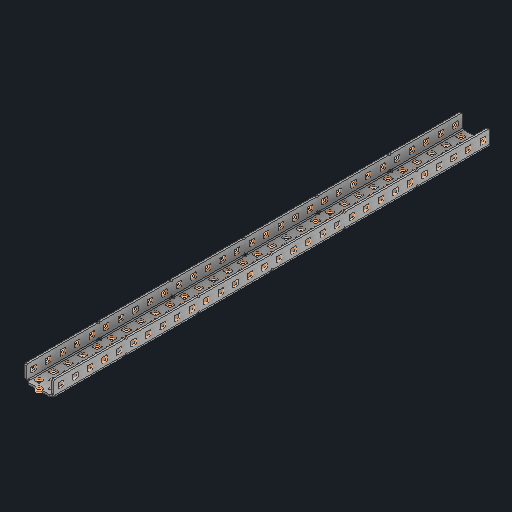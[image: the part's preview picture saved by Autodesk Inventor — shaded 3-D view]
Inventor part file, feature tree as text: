
AUTODESK INVENTOR PART (.ipt)
format: ipt  version: 2025 (Build 290162000, 162)  size: 2,433,536 bytes
history: native  units: in
note: dims shown in document units (in); Inventor stores cm internally (conversion verified against a paired STEP export)
features: other x306, sketch x5, sheet_metal_op x1
ambient origin geometry x8: Origin, YZ Plane, XZ Plane, XY Plane, X Axis, Y Axis, Z Axis, Center Point
bodies: Solid1 (feature_tree)
feature tree (312):
  other  "Alu C 1x2x1x30.ipt"
  other  "Solid1::Alu C 1x2x1x30.ipt"
  other  "TaggingFeature1"
  sketch  "Sketch1"  dims[d0=0.3937in]
  sketch  "Sketch2"  dims[d1=0.0625in]
  sketch  "Sketch3"
  other  "Flange Pattern Sketch"
  sketch  "Sketch9"
  sheet_metal_op  "Body Pattern Sketch"
  other  "Arc Length"
  sketch  "Sketch14"
  other  "Flange Pattern Plane"
  other  "Srf1"
  other  "Srf2"
  other  "Srf3"
  other  "Srf4"
  other  "Srf5"
  other  "Srf6"
  other  "Srf7"
  other  "Srf8"
  other  "Srf9"
  other  "Srf10"
  other  "Srf11"
  other  "Srf12"
  other  "Srf13"
  other  "Srf14"
  other  "Srf15"
  other  "Srf16"
  other  "Srf17"
  other  "Srf18"
  other  "Srf19"
  other  "Srf20"
  other  "Srf21"
  other  "Srf22"
  other  "Srf23"
  other  "Srf24"
  other  "Srf25"
  other  "Srf26"
  other  "Srf27"
  other  "Srf28"
  other  "Srf29"
  other  "Srf30"
  other  "Srf31"
  other  "Srf32"
  other  "Srf33"
  other  "Srf34"
  other  "Srf35"
  other  "Srf36"
  other  "Srf37"
  other  "Srf38"
  other  "Srf39"
  other  "Srf40"
  other  "Srf41"
  other  "Srf42"
  other  "Srf43"
  other  "Srf44"
  other  "Srf45"
  other  "Srf46"
  other  "Srf47"
  other  "Srf48"
  other  "Srf49"
  other  "Srf50"
  other  "Srf51"
  other  "Srf52"
  other  "Srf53"
  other  "Srf54"
  other  "Srf55"
  other  "Srf56"
  other  "Srf57"
  other  "Srf58"
  other  "Srf59"
  other  "Srf60"
  other  "Srf61"
  other  "Srf62"
  other  "Srf63"
  other  "Srf64"
  other  "Srf65"
  other  "Srf66"
  other  "Srf67"
  other  "Srf68"
  other  "Srf69"
  other  "Srf70"
  other  "Srf71"
  other  "Srf72"
  other  "Srf73"
  other  "Srf74"
  other  "Srf75"
  other  "Srf76"
  other  "Srf77"
  other  "Srf78"
  other  "Srf79"
  other  "Srf80"
  other  "Srf81"
  other  "Srf82"
  other  "Srf83"
  other  "Srf84"
  other  "Srf85"
  other  "Srf86"
  other  "Srf87"
  other  "Srf88"
  other  "Srf89"
  other  "Srf90"
  other  "Srf91"
  other  "Srf92"
  other  "Srf93"
  other  "Srf94"
  other  "Srf95"
  other  "Srf96"
  other  "Srf97"
  other  "Srf98"
  other  "Srf99"
  other  "Srf100"
  other  "Srf101"
  other  "Srf102"
  other  "Srf103"
  other  "Srf104"
  other  "Srf105"
  other  "Srf106"
  other  "Srf107"
  other  "Srf108"
  other  "Srf109"
  other  "Srf110"
  other  "Srf111"
  other  "Srf112"
  other  "Srf113"
  other  "Srf114"
  other  "Srf115"
  other  "Srf116"
  other  "Srf117"
  other  "Srf118"
  other  "Srf119"
  other  "Srf120"
  other  "Srf121"
  other  "Srf122"
  other  "Srf123"
  other  "Srf124"
  other  "Srf125"
  other  "Srf126"
  other  "Srf127"
  other  "Srf128"
  other  "Srf129"
  other  "Srf130"
  other  "Srf131"
  other  "Srf132"
  other  "Srf133"
  other  "Srf134"
  other  "Srf135"
  other  "Srf136"
  other  "Srf137"
  other  "Srf138"
  other  "Srf139"
  other  "Srf140"
  other  "Srf141"
  other  "Srf142"
  other  "Srf143"
  other  "Srf144"
  other  "Srf145"
  other  "Srf146"
  other  "Srf147"
  other  "Srf148"
  other  "Srf149"
  other  "Srf150"
  other  "Srf1::Derived"
  other  "Srf2::Derived"
  other  "Srf823::Derived"
  other  "Srf824::Derived"
  other  "Srf825::Derived"
  other  "Srf826::Derived"
  other  "Srf827::Derived"
  other  "Srf828::Derived"
  other  "Srf829::Derived"
  other  "Srf922::Derived"
  other  "Srf923::Derived"
  other  "Srf924::Derived"
  other  "Srf925::Derived"
  other  "Srf926::Derived"
  other  "Srf1143::Derived"
  other  "Srf1144::Derived"
  other  "Srf1145::Derived"
  other  "Srf1146::Derived"
  other  "Srf1147::Derived"
  other  "Srf1148::Derived"
  other  "Srf1149::Derived"
  other  "Srf1150::Derived"
  other  "Srf1151::Derived"
  other  "Srf1152::Derived"
  other  "Srf1153::Derived"
  other  "Srf1154::Derived"
  other  "Srf1155::Derived"
  other  "Srf1156::Derived"
  other  "Srf1157::Derived"
  other  "Srf1158::Derived"
  other  "Srf1159::Derived"
  other  "Srf1160::Derived"
  other  "Srf1161::Derived"
  other  "Srf1162::Derived"
  other  "Srf1163::Derived"
  other  "Srf1164::Derived"
  other  "Srf1165::Derived"
  other  "Srf1166::Derived"
  other  "Srf1167::Derived"
  other  "Srf1168::Derived"
  other  "Srf1169::Derived"
  other  "Srf1170::Derived"
  other  "Srf1171::Derived"
  other  "Srf1172::Derived"
  other  "Srf1173::Derived"
  other  "Srf1174::Derived"
  other  "Srf1175::Derived"
  other  "Srf1176::Derived"
  other  "Srf1177::Derived"
  other  "Srf1178::Derived"
  other  "Srf1179::Derived"
  other  "Srf1180::Derived"
  other  "Srf1181::Derived"
  other  "Srf1182::Derived"
  other  "Srf1183::Derived"
  other  "Srf1184::Derived"
  other  "Srf1185::Derived"
  other  "Srf1186::Derived"
  other  "Srf1187::Derived"
  other  "Srf1188::Derived"
  other  "Srf91::Derived"
  other  "Srf92::Derived"
  other  "Srf856::Derived"
  other  "Srf857::Derived"
  other  "Srf858::Derived"
  other  "Srf859::Derived"
  other  "Srf860::Derived"
  other  "Srf861::Derived"
  other  "Srf862::Derived"
  other  "Srf959::Derived"
  other  "Srf960::Derived"
  other  "Srf961::Derived"
  other  "Srf962::Derived"
  other  "Srf963::Derived"
  other  "Srf1199::Derived"
  other  "Srf1200::Derived"
  other  "Srf1201::Derived"
  other  "Srf1202::Derived"
  other  "Srf1203::Derived"
  other  "Srf1204::Derived"
  other  "Srf1205::Derived"
  other  "Srf1206::Derived"
  other  "Srf1207::Derived"
  other  "Srf1208::Derived"
  other  "Srf1209::Derived"
  other  "Srf1210::Derived"
  other  "Srf1211::Derived"
  other  "Srf1212::Derived"
  other  "Srf1213::Derived"
  other  "Srf1214::Derived"
  other  "Srf1215::Derived"
  other  "Srf1216::Derived"
  other  "Srf1217::Derived"
  other  "Srf1218::Derived"
  other  "Srf1219::Derived"
  other  "Srf1220::Derived"
  other  "Srf1221::Derived"
  other  "Srf1222::Derived"
  other  "Srf1223::Derived"
  other  "Srf1224::Derived"
  other  "Srf1225::Derived"
  other  "Srf1226::Derived"
  other  "Srf1227::Derived"
  other  "Srf1228::Derived"
  other  "Srf1229::Derived"
  other  "Srf1230::Derived"
  other  "Srf1231::Derived"
  other  "Srf1232::Derived"
  other  "Srf1233::Derived"
  other  "Srf1234::Derived"
  other  "Srf1235::Derived"
  other  "Srf1236::Derived"
  other  "Srf1237::Derived"
  other  "Srf1238::Derived"
  other  "Srf1239::Derived"
  other  "Srf1240::Derived"
  other  "Srf1241::Derived"
  other  "Srf1242::Derived"
  other  "Srf1243::Derived"
  other  "Srf1244::Derived"
  other  "Srf786::Derived"
  other  "Srf889::Derived"
  other  "Srf890::Derived"
  other  "Srf891::Derived"
  other  "Srf892::Derived"
  other  "Srf893::Derived"
  other  "Srf894::Derived"
  other  "Srf895::Derived"
  other  "Srf896::Derived"
  other  "Srf996::Derived"
  other  "Srf997::Derived"
  other  "Srf998::Derived"
  other  "Srf999::Derived"
  other  "Srf1000::Derived"
  other  "Srf1255::Derived"
  other  "Srf1256::Derived"
  other  "Srf1257::Derived"
  other  "Srf1258::Derived"
  other  "Srf1259::Derived"
  other  "Srf1260::Derived"
  other  "Srf1261::Derived"
  other  "Srf1262::Derived"
  other  "Srf1263::Derived"
  other  "Srf1264::Derived"
  other  "Srf1265::Derived"
  other  "Srf1266::Derived"
  other  "Srf1267::Derived"
  other  "Srf1268::Derived"
  other  "Srf1269::Derived"
  other  "Srf1270::Derived"
